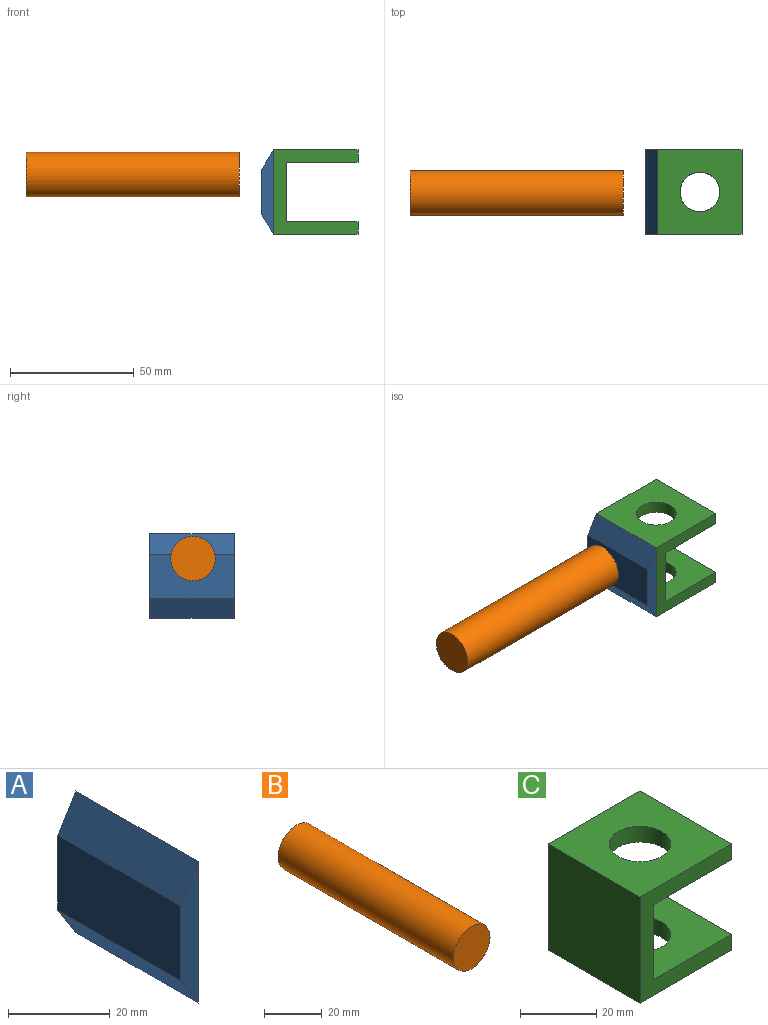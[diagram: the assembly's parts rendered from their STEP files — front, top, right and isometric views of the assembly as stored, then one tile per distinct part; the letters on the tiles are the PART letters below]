
ASSEMBLY  parts=3 mates=3
PART A: 6 faces, bbox 5x34x34 mm
  f0: plane 34x8.15mm, normal (-0.85,0,0.52), area 325mm2, adj f1,f3,f4,f5
  f1: plane 34x18mm, normal (-1,0,0), area 612mm2, adj f0,f2,f4,f5
  f2: plane 34x7.85mm, normal (-0.84,0,-0.54), area 316.5mm2, adj f1,f3,f4,f5
  f3: plane 34x34mm, normal (1,0,0), area 1156mm2, adj f0,f2,f4,f5
  f4: plane 34x5mm, normal (0,-1,0), area 130mm2, adj f0,f1,f2,f3
  f5: plane 34x5mm, normal (0,1,0), area 130mm2, adj f0,f1,f2,f3
PART B: 3 faces, bbox 18x86x18 mm
  f0: cylinder r=9mm len=86mm, axis (0,1,0), area 4863.2mm2, adj f1,f2
  f1: plane 18x18mm, normal (0,-1,0), area 254.5mm2, adj f0
  f2: plane 18x18mm, normal (0,1,0), area 254.5mm2, adj f0
PART C: 12 faces, bbox 34x34x34 mm
  f0: plane 34x34mm, normal (-1,0,0), area 1156mm2, adj f1,f7,f8,f9
  f1: plane 34x34mm, normal (0,0,-1), area 954.9mm2, adj f0,f2,f8,f9,f11
  f2: plane 34x5mm, normal (1,0,0), area 170mm2, adj f1,f3,f8,f9
  f3: plane 34x29mm, normal (0,0,1), area 784.9mm2, adj f2,f4,f8,f9,f11
  f4: plane 34x24mm, normal (1,0,0), area 816mm2, adj f3,f5,f8,f9
  f5: plane 34x29mm, normal (0,0,-1), area 784.9mm2, adj f4,f6,f8,f9,f10
  f6: plane 34x5mm, normal (1,0,0), area 170mm2, adj f5,f7,f8,f9
  f7: plane 34x34mm, normal (0,0,1), area 954.9mm2, adj f0,f6,f8,f9,f10
  f8: plane 34x34mm, normal (0,-1,0), area 460mm2, adj f0,f1,f2,f3,f4,f5,f6,f7
  f9: plane 34x34mm, normal (0,1,0), area 460mm2, adj f0,f1,f2,f3,f4,f5,f6,f7
  f10: cylinder r=8mm len=16mm, axis (0,0,-1), area 251.3mm2, adj f5,f7
  f11: cylinder r=8mm len=16mm, axis (0,0,-1), area 251.3mm2, adj f1,f3
PLACE A t=(-4.68,-33.99,0.68)mm
PLACE B rot(axis=(0,0,1),90deg) t=(-170.83,10.79,-24.61)mm
PLACE C t=(-35.49,-33.99,-22.52)mm
MATE parallel B.f0 <-> A.f1  axis (1,0,0) through (-84.83,-51.38,9.14)mm
MATE parallel A.f3 <-> C.f0  axis (1,0,0) through (-70.84,-50.99,2.1)mm
MATE parallel C.f0 <-> A.f3  axis (-1,0,0) through (-70.84,-50.99,2.1)mm
